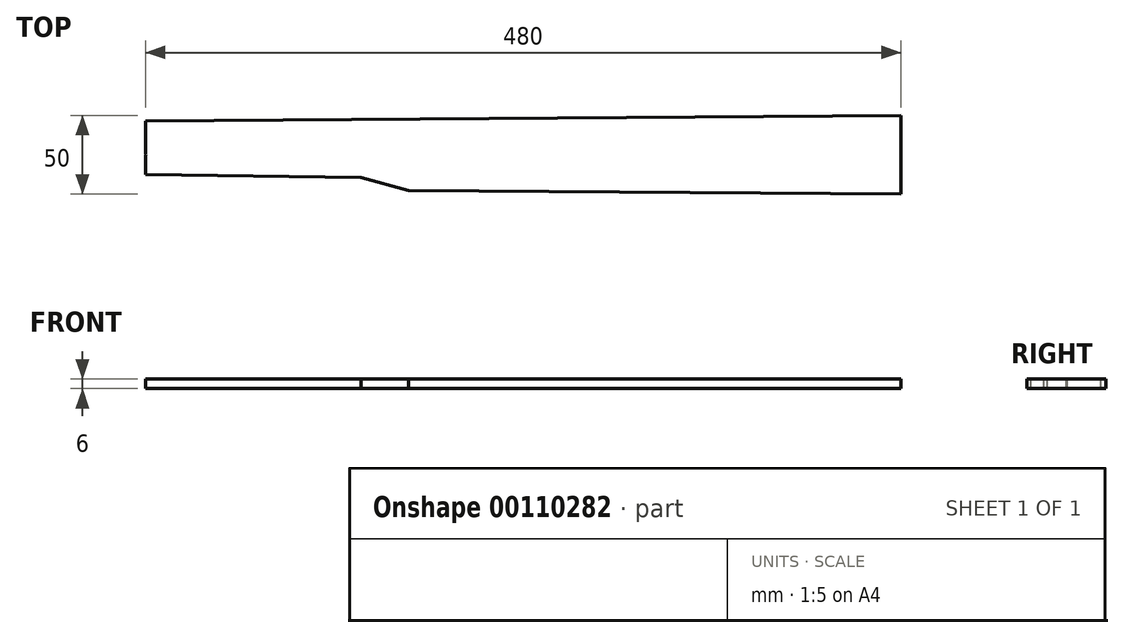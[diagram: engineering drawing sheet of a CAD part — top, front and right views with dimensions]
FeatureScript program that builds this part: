
annotation { "Feature Type Name" : "Feature", "Feature Type Description" : "" }
export const myFeature = defineFeature(function(context is Context, id is Id, definition is map)
    precondition{}
    {
        {
            var Q0;
            Q0=qCreatedBy(makeId("Top.planeOp"),FACE);
            var sketch = newSketch(context, id + "F0", { "sketchPlane" : qUnion([Q0])});
            skLineSegment(sketch, "E0", {"start": v(0, -0.34) * mm, "end": v(0, -12.5) * mm});
            skLineSegment(sketch, "E1", {"start": v(480, 16) * mm, "end": v(480, 25) * mm});
            skLineSegment(sketch, "E2", {"start": v(0, 0) * mm, "end": v(542, 0) * mm, "construction": true});
            skLineSegment(sketch, "E3", {"start": v(480, 25) * mm, "end": v(480, 0) * mm});
            skPoint(sketch, "E4", {"position": v(0, 18) * mm});
            skPoint(sketch, "E5", {"position": v(0, 9) * mm});
            skPoint(sketch, "E6", {"position": v(0, -9) * mm});
            skPoint(sketch, "E7", {"position": v(167, -52.28) * mm});
            skLineSegment(sketch, "E8", {"start": v(137, 51.44) * mm, "end": v(137, -57.6) * mm, "construction": true});
            skPoint(sketch, "E9", {"position": v(0, 21.5) * mm});
            skLineSegment(sketch, "E10", {"start": v(0, 21.5) * mm, "end": v(480, 25) * mm});
            skLineSegment(sketch, "E11", {"start": v(167, -52.28) * mm, "end": v(167, 81.51) * mm, "construction": true});
            skPoint(sketch, "E12", {"position": v(137, 22.5) * mm});
            skPoint(sketch, "E13", {"position": v(167, 22.72) * mm});
            skLineSegment(sketch, "E14", {"start": v(0, 18) * mm, "end": v(0, 0.35) * mm});
            skLineSegment(sketch, "E15", {"start": v(0, 21.5) * mm, "end": v(0, 18) * mm});
            skLineSegment(sketch, "E16", {"start": v(0, -12.5) * mm, "end": v(0, -0.34) * mm});
            skPoint(sketch, "E17", {"position": v(0, 0) * mm});
            skLineSegment(sketch, "E18", {"start": v(0.35, 0) * mm, "end": v(0, -0.34) * mm});
            skLineSegment(sketch, "E19", {"start": v(0.35, 0) * mm, "end": v(0, 0.35) * mm});
            skPoint(sketch, "E20", {"position": v(167, 0) * mm});
            skLineSegment(sketch, "E21.MirrorCS", {"start": v(167, -22.72) * mm, "end": v(480, -25) * mm});
            skLineSegment(sketch, "E22.MirrorCS", {"start": v(480, -25) * mm, "end": v(480, 0) * mm});
            skPoint(sketch, "E23", {"position": v(137, -14.5) * mm});
            skPoint(sketch, "E24", {"position": v(167, -22.72) * mm});
            skLineSegment(sketch, "E25", {"start": v(0, -12.5) * mm, "end": v(137, -14.5) * mm});
            skLineSegment(sketch, "E26", {"start": v(137, -14.5) * mm, "end": v(167, -22.72) * mm});
            skSolve(sketch);
        }
        {
            var Q0;
            Q0 = qSketchRegion(id + "F0", true);
            extrude(context, id + "F1", {"entities" : qUnion([Q0]), "depth" : 6 * mm});
        }
    });
